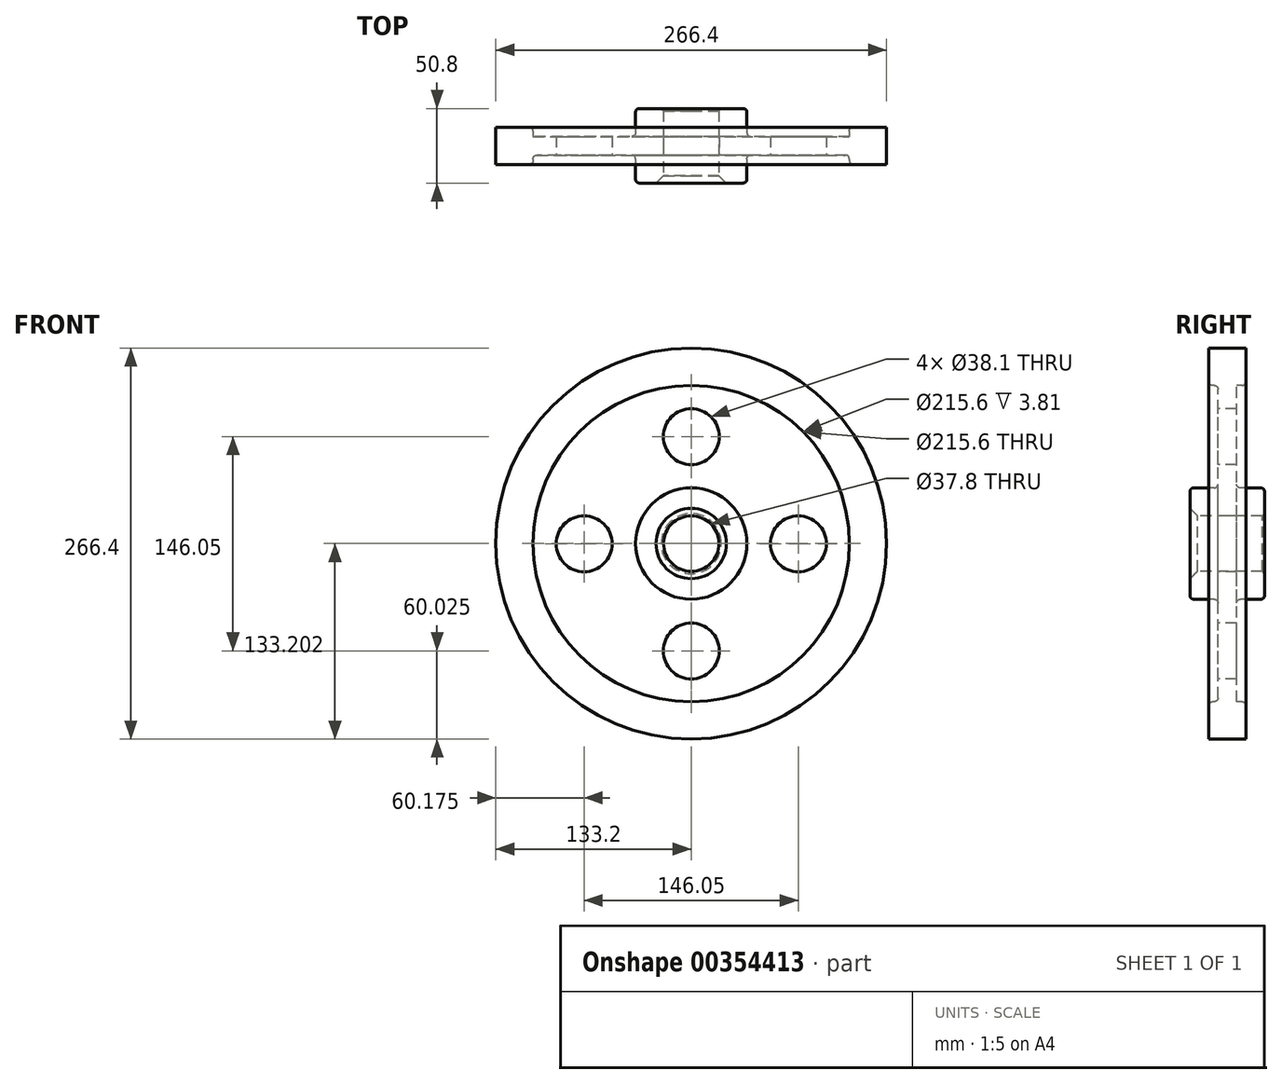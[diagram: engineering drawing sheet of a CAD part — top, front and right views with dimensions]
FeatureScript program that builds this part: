
annotation { "Feature Type Name" : "Feature", "Feature Type Description" : "" }
export const myFeature = defineFeature(function(context is Context, id is Id, definition is map)
    precondition{}
    {
        {
            var Q0;
            Q0=qCreatedBy(makeId("Right.planeOp"),FACE);
            var sketch = newSketch(context, id + "F0", { "sketchPlane" : qUnion([Q0])});
            skLineSegment(sketch, "E0", {"start": v(0, 0) * mm, "end": v(74.68, 0) * mm, "construction": true});
            skLineSegment(sketch, "E1.0", {"start": v(0, 19.05) * mm, "end": v(25.4, 19.05) * mm});
            skLineSegment(sketch, "E2.0", {"start": v(6.35, 38.1) * mm, "end": v(25.4, 38.1) * mm});
            skLineSegment(sketch, "E3.0", {"start": v(6.35, 107.95) * mm, "end": v(12.7, 107.95) * mm});
            skLineSegment(sketch, "E4.0", {"start": v(0, 0.15) * mm, "end": v(74.68, 0.15) * mm});
            skLineSegment(sketch, "E5.0", {"start": v(0, 133.35) * mm, "end": v(12.7, 133.35) * mm});
            skLineSegment(sketch, "E6", {"start": v(0, 0) * mm, "end": v(0, 133.35) * mm, "construction": true});
            skLineSegment(sketch, "E7", {"start": v(0, 0.15) * mm, "end": v(25.4, 0.15) * mm, "construction": true});
            skLineSegment(sketch, "E8.0", {"start": v(25.4, 0) * mm, "end": v(25.4, 0.15) * mm});
            skLineSegment(sketch, "E9.0", {"start": v(6.35, 0) * mm, "end": v(6.35, 0.15) * mm});
            skLineSegment(sketch, "E10.0", {"start": v(12.7, 0) * mm, "end": v(12.7, 0.15) * mm});
            skPoint(sketch, "E11.orphan", {"position": v(0, -74.22) * mm});
            skLineSegment(sketch, "E12.trimOffspring", {"start": v(25.4, 19.05) * mm, "end": v(25.4, 38.1) * mm});
            skLineSegment(sketch, "E13.trimOffspring", {"start": v(6.35, 38.1) * mm, "end": v(6.35, 107.95) * mm});
            skLineSegment(sketch, "E14.trimOffspring", {"start": v(12.7, 107.95) * mm, "end": v(12.7, 133.35) * mm});
            skLineSegment(sketch, "E15.MirrorCS", {"start": v(-12.7, 107.95) * mm, "end": v(-12.7, 133.35) * mm});
            skLineSegment(sketch, "E16.MirrorCS", {"start": v(-6.35, 38.1) * mm, "end": v(-6.35, 107.95) * mm});
            skLineSegment(sketch, "E17.MirrorCS", {"start": v(-25.4, 19.05) * mm, "end": v(-25.4, 38.1) * mm});
            skLineSegment(sketch, "E18.MirrorCS", {"start": v(-6.35, 38.1) * mm, "end": v(-25.4, 38.1) * mm});
            skLineSegment(sketch, "E19.MirrorCS", {"start": v(0, 19.05) * mm, "end": v(-25.4, 19.05) * mm});
            skLineSegment(sketch, "E20.MirrorCS", {"start": v(0, 133.35) * mm, "end": v(-12.7, 133.35) * mm});
            skLineSegment(sketch, "E21.MirrorCS", {"start": v(-6.35, 107.95) * mm, "end": v(-12.7, 107.95) * mm});
            skSolve(sketch);
        }
        {
            var Q0;
            Q0=makeQuery(id+"F0.imprint","IMPRINT",FACE,{"disambiguationData":[TD([[makeQuery(id+"F0.imprint","IMPRINT",EDGE,{"derivedFrom":sQuery(id+"F0.wireOp",EDGE,"E1.0")}),1.0]])]});
            var Q1;
            Q1=sQuery(id+"F0.wireOp",EDGE,"E4.0");
            revolve(context, id + "F1", {"entities" : qUnion([Q0]), "axis" : qUnion([Q1]), "revolveType" : RevolveType.FULL});
        }
        {
            var Q0;
            Q0=makeQuery(id+"F1.opRevolve","SWEPT_FACE",FACE,{"disambiguationData":[OSD([sQuery(id+"F0.wireOp",EDGE,"E15.MirrorCS")])]});
            var sketch = newSketch(context, id + "F2", { "sketchPlane" : qUnion([Q0])});
            skLineSegment(sketch, "E22", {"start": v(0, 0) * mm, "end": v(0, 73.03) * mm});
            skCircle(sketch, "E23", {"center": v(0, 73.03) * mm, "radius": 19.05 * mm});
            skCircle(sketch, "E24.1.0", {"center": v(-73.03, 0) * mm, "radius": 19.05 * mm});
            skCircle(sketch, "E24.2.0", {"center": v(0, -73.03) * mm, "radius": 19.05 * mm});
            skCircle(sketch, "E24.3.0", {"center": v(73.03, 0) * mm, "radius": 19.05 * mm});
            skPoint(sketch, "E24.center", {"position": v(0, 0) * mm});
            skSolve(sketch);
        }
        {
            var Q0;
            Q0=makeQuery(id+"F2.imprint","IMPRINT",FACE,{"disambiguationData":[TD([[makeQuery(id+"F2.imprint","IMPRINT",EDGE,{"derivedFrom":sQuery(id+"F2.wireOp",EDGE,"E24.3.0")}),1.0]])]});
            var Q1;
            Q1=makeQuery(id+"F2.imprint","IMPRINT",FACE,{"disambiguationData":[TD([[makeQuery(id+"F2.imprint","IMPRINT",EDGE,{"derivedFrom":sQuery(id+"F2.wireOp",EDGE,"E23")}),1.0]])]});
            var Q2;
            Q2=makeQuery(id+"F2.imprint","IMPRINT",FACE,{"disambiguationData":[TD([[makeQuery(id+"F2.imprint","IMPRINT",EDGE,{"derivedFrom":sQuery(id+"F2.wireOp",EDGE,"E24.1.0")}),1.0]])]});
            var Q3;
            Q3=makeQuery(id+"F2.imprint","IMPRINT",FACE,{"disambiguationData":[TD([[makeQuery(id+"F2.imprint","IMPRINT",EDGE,{"derivedFrom":sQuery(id+"F2.wireOp",EDGE,"E24.2.0")}),1.0]])]});
            extrude(context, id + "F3", {"entities" : qUnion([Q0, Q1, Q2, Q3]), "operationType" : NewBodyOperationType.REMOVE, "oppositeDirection" : true, "depth" : 25.4 * mm});
        }
        {
            var Q0;
            Q0=makeQuery(id+"F1.opRevolve","SWEPT_EDGE",EDGE,{"disambiguationData":[OSD([sQuery(id+"F0.wireOp",EDGE,"E3.0"),sQuery(id+"F0.wireOp",EDGE,"E14.trimOffspring")])]});
            var Q1;
            Q1=makeQuery(id+"F1.opRevolve","SWEPT_EDGE",EDGE,{"disambiguationData":[OSD([sQuery(id+"F0.wireOp",EDGE,"E2.0"),sQuery(id+"F0.wireOp",EDGE,"E12.trimOffspring")])]});
            var Q2;
            Q2=makeQuery(id+"F1.opRevolve","SWEPT_EDGE",EDGE,{"disambiguationData":[OSD([sQuery(id+"F0.wireOp",EDGE,"E2.0"),sQuery(id+"F0.wireOp",EDGE,"E13.trimOffspring")])]});
            fillet(context, id + "F4", {"entities" : qUnion([Q0, Q1, Q2]), "radius" : 2.54 * mm, "tangentPropagation" : true, "allowEdgeOverflow" : false});
        }
        {
            var Q0;
            Q0=makeQuery(id+"F1.opRevolve","SWEPT_EDGE",EDGE,{"disambiguationData":[OSD([sQuery(id+"F0.wireOp",EDGE,"E17.MirrorCS"),sQuery(id+"F0.wireOp",EDGE,"E18.MirrorCS")])]});
            var Q1;
            Q1=makeQuery(id+"F1.opRevolve","SWEPT_EDGE",EDGE,{"disambiguationData":[OSD([sQuery(id+"F0.wireOp",EDGE,"E16.MirrorCS"),sQuery(id+"F0.wireOp",EDGE,"E18.MirrorCS")])]});
            var Q2;
            Q2=makeQuery(id+"F1.opRevolve","SWEPT_EDGE",EDGE,{"disambiguationData":[OSD([sQuery(id+"F0.wireOp",EDGE,"E15.MirrorCS"),sQuery(id+"F0.wireOp",EDGE,"E21.MirrorCS")])]});
            var Q3;
            Q3=makeQuery(id+"F1.opRevolve","SWEPT_EDGE",EDGE,{"disambiguationData":[OSD([sQuery(id+"F0.wireOp",EDGE,"E16.MirrorCS"),sQuery(id+"F0.wireOp",EDGE,"E21.MirrorCS")])]});
            fillet(context, id + "F5", {"entities" : qUnion([Q0, Q1, Q2, Q3]), "radius" : 2.54 * mm, "tangentPropagation" : true, "allowEdgeOverflow" : false});
        }
        {
            var Q0;
            Q0=makeQuery(id+"F1.opRevolve","SWEPT_EDGE",EDGE,{"disambiguationData":[OSD([sQuery(id+"F0.wireOp",EDGE,"E1.0"),sQuery(id+"F0.wireOp",EDGE,"E12.trimOffspring")])]});
            chamfer(context, id + "F6", {"entities" : qUnion([Q0]), "width" : 1.59 * mm, "tangentPropagation" : true});
        }
        {
            var Q0;
            Q0=makeQuery(id+"F1.opRevolve","SWEPT_EDGE",EDGE,{"disambiguationData":[OSD([sQuery(id+"F0.wireOp",EDGE,"E17.MirrorCS"),sQuery(id+"F0.wireOp",EDGE,"E19.MirrorCS")])]});
            chamfer(context, id + "F7", {"entities" : qUnion([Q0]), "width" : 5.08 * mm, "tangentPropagation" : true});
        }
    });
